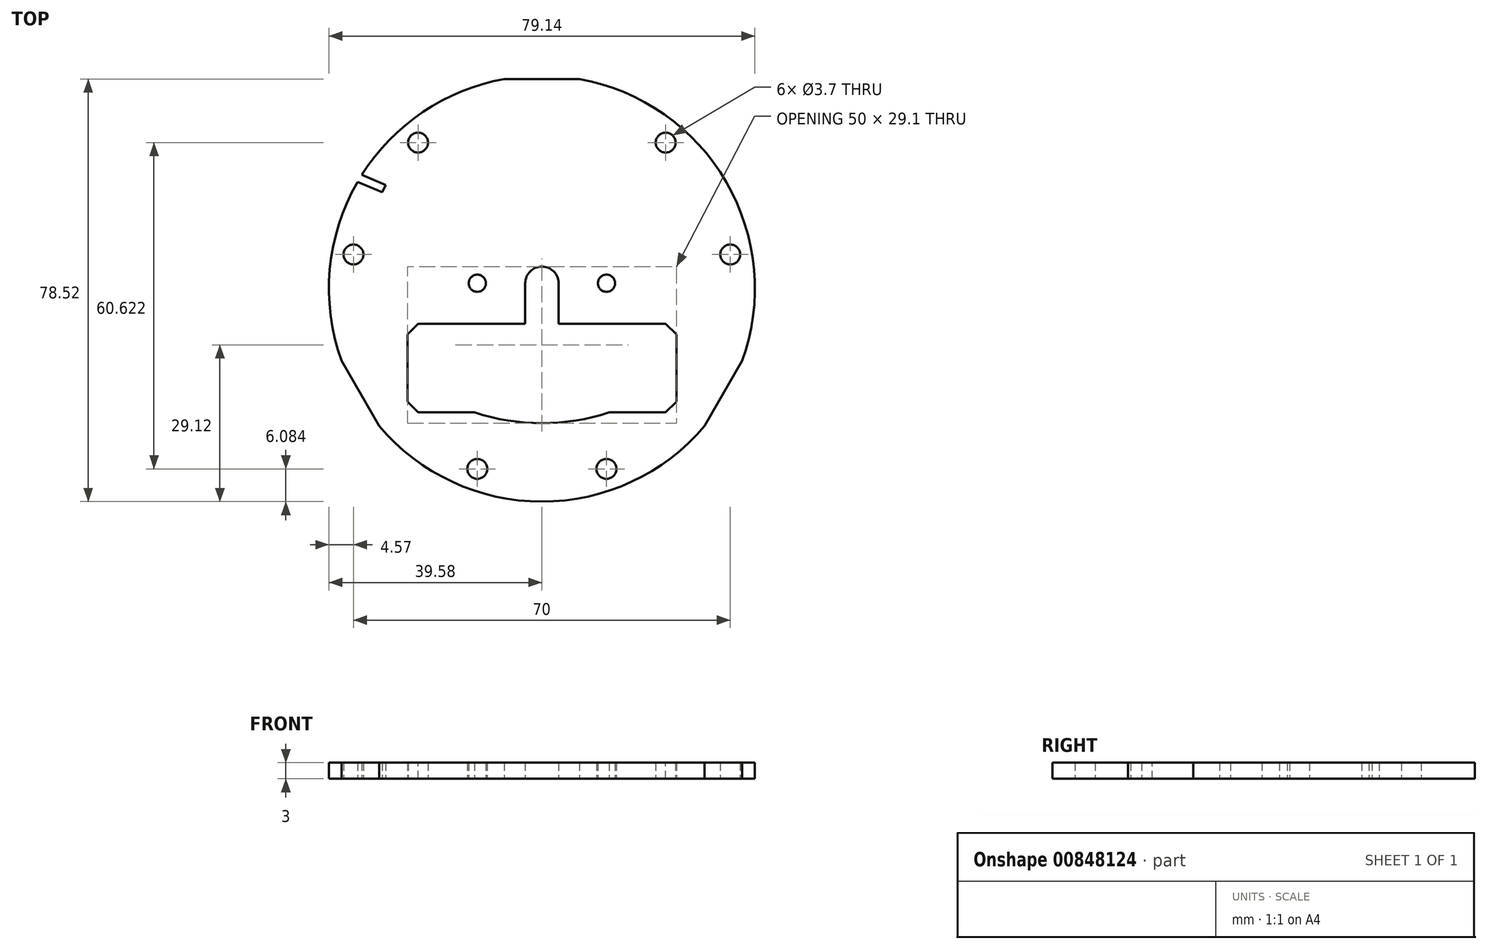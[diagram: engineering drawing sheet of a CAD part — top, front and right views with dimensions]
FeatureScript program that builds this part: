
annotation { "Feature Type Name" : "Feature", "Feature Type Description" : "" }
export const myFeature = defineFeature(function(context is Context, id is Id, definition is map)
    precondition{}
    {
        {
            var Q0;
            Q0=qCreatedBy(makeId("Top.planeOp"),FACE);
            var sketch = newSketch(context, id + "F0", { "sketchPlane" : qUnion([Q0])});
            skLineSegment(sketch, "E0.bottom", {"start": v(25, -7.5) * mm, "end": v(-25, -7.5) * mm});
            skLineSegment(sketch, "E0.top", {"start": v(25, -24) * mm, "end": v(-25, -24) * mm});
            skLineSegment(sketch, "E0.left", {"start": v(25, -7.5) * mm, "end": v(25, -24) * mm});
            skLineSegment(sketch, "E0.right", {"start": v(-25, -7.5) * mm, "end": v(-25, -24) * mm});
            skPoint(sketch, "E0.middle", {"position": v(0, -15.75) * mm});
            skArc(sketch, "E1", {"start": v(3.1, 0) * mm, "mid": v(0, 3.1) * mm, "end": v(-3.1, 0) * mm});
            skLineSegment(sketch, "E2", {"start": v(-3.1, 0) * mm, "end": v(-3.1, -7.5) * mm});
            skLineSegment(sketch, "E3", {"start": v(3.1, 0) * mm, "end": v(3.1, -7.5) * mm});
            skCircle(sketch, "E4", {"center": v(-12, 0) * mm, "radius": 1.6 * mm});
            skCircle(sketch, "E5", {"center": v(12, 0) * mm, "radius": 1.6 * mm});
            skCircle(sketch, "E6", {"center": v(0, -1) * mm, "radius": 45 * mm, "construction": true});
            skLineSegment(sketch, "E7", {"start": v(0, -1) * mm, "end": v(-38.98, -23.5) * mm, "construction": true});
            skCircle(sketch, "E8", {"center": v(-12, -34.49) * mm, "radius": 1.85 * mm});
            skCircle(sketch, "E9.MirrorC", {"center": v(-35, 5.35) * mm, "radius": 1.85 * mm});
            skLineSegment(sketch, "E10", {"start": v(-30.24, -26.54) * mm, "end": v(-37.24, -14.41) * mm});
            skLineSegment(sketch, "E11.1.0", {"start": v(37.22, -14.41) * mm, "end": v(30.22, -26.54) * mm});
            skCircle(sketch, "E11.1.1", {"center": v(34.99, 5.35) * mm, "radius": 1.85 * mm});
            skCircle(sketch, "E11.1.2", {"center": v(12, -34.49) * mm, "radius": 1.85 * mm});
            skLineSegment(sketch, "E11.2.0", {"start": v(-7.01, 37.95) * mm, "end": v(6.99, 37.95) * mm});
            skCircle(sketch, "E11.2.1", {"center": v(-23.01, 26.14) * mm, "radius": 1.85 * mm});
            skCircle(sketch, "E11.2.2", {"center": v(22.99, 26.14) * mm, "radius": 1.85 * mm});
            skCircle(sketch, "E12", {"center": v(0, -1) * mm, "radius": 39.57 * mm});
            skCircle(sketch, "E13", {"center": v(-12, -34.49) * mm, "radius": 5 * mm, "construction": true});
            skCircle(sketch, "E14", {"center": v(12, -34.49) * mm, "radius": 5 * mm, "construction": true});
            skLineSegment(sketch, "E15.bottom", {"start": v(-18.5, -1.5) * mm, "end": v(-21.5, -1.5) * mm});
            skLineSegment(sketch, "E15.top", {"start": v(-18.5, 3.5) * mm, "end": v(-21.5, 3.5) * mm});
            skLineSegment(sketch, "E15.left", {"start": v(-18.5, -1.5) * mm, "end": v(-18.5, 3.5) * mm});
            skLineSegment(sketch, "E15.right", {"start": v(-21.5, -1.5) * mm, "end": v(-21.5, 3.5) * mm, "construction": true});
            skPoint(sketch, "E15.middle", {"position": v(-20, 1) * mm});
            skLineSegment(sketch, "E16", {"start": v(0, 0) * mm, "end": v(0, -1) * mm, "construction": true});
            skLineSegment(sketch, "E17", {"start": v(0, 0) * mm, "end": v(0, 3.1) * mm, "construction": true});
            skLineSegment(sketch, "E18.MirrorCS", {"start": v(18.5, -1.5) * mm, "end": v(18.5, 3.5) * mm});
            skLineSegment(sketch, "E19.MirrorCS", {"start": v(18.5, -1.5) * mm, "end": v(21.5, -1.5) * mm});
            skLineSegment(sketch, "E20.MirrorCS", {"start": v(21.5, -1.5) * mm, "end": v(21.5, 3.5) * mm, "construction": true});
            skLineSegment(sketch, "E21.MirrorCS", {"start": v(18.5, 3.5) * mm, "end": v(21.5, 3.5) * mm});
            skArc(sketch, "E22", {"start": v(-12.5, -24) * mm, "mid": v(0, -26) * mm, "end": v(12.5, -24) * mm});
            skLineSegment(sketch, "E23", {"start": v(-34.25, 18.83) * mm, "end": v(-29.65, 16.9) * mm});
            skLineSegment(sketch, "E24", {"start": v(-29.65, 16.9) * mm, "end": v(-29.06, 18.27) * mm});
            skLineSegment(sketch, "E25", {"start": v(-29.06, 18.27) * mm, "end": v(-33.47, 20.13) * mm});
            skSolve(sketch);
        }
        {
            var Q0;
            {var subQ3=sQuery(id+"F0.wireOp",EDGE,"E0.left");Q0=makeQuery(id+"F0.imprint","IMPRINT",FACE,{"disambiguationData":[TD([[makeQuery(id+"F0.imprint","IMPRINT",EDGE,{"derivedFrom":subQ3}),1.0]])]});}
            extrude(context, id + "F1", {"entities" : qUnion([Q0]), "depth" : 3 * mm, "offsetDistance" : 25 * mm});
        }
        {
            var Q0;
            Q0=makeQuery(id+"F1.opExtrude","SWEPT_EDGE",EDGE,{"disambiguationData":[OSD([sQuery(id+"F0.wireOp",EDGE,"E0.top"),sQuery(id+"F0.wireOp",EDGE,"E0.right")])]});
            var Q1;
            Q1=makeQuery(id+"F1.opExtrude","SWEPT_EDGE",EDGE,{"disambiguationData":[OSD([sQuery(id+"F0.wireOp",EDGE,"E0.top"),sQuery(id+"F0.wireOp",EDGE,"E0.left")])]});
            var Q2;
            Q2=makeQuery(id+"F1.opExtrude","SWEPT_EDGE",EDGE,{"disambiguationData":[OSD([sQuery(id+"F0.wireOp",EDGE,"E0.bottom"),sQuery(id+"F0.wireOp",EDGE,"E0.right")])]});
            var Q3;
            Q3=makeQuery(id+"F1.opExtrude","SWEPT_EDGE",EDGE,{"disambiguationData":[OSD([sQuery(id+"F0.wireOp",EDGE,"E0.bottom"),sQuery(id+"F0.wireOp",EDGE,"E0.left")])]});
            chamfer(context, id + "F2", {"entities" : qUnion([Q0, Q1, Q2, Q3]), "width" : 2 * mm, "tangentPropagation" : true});
        }
    });
